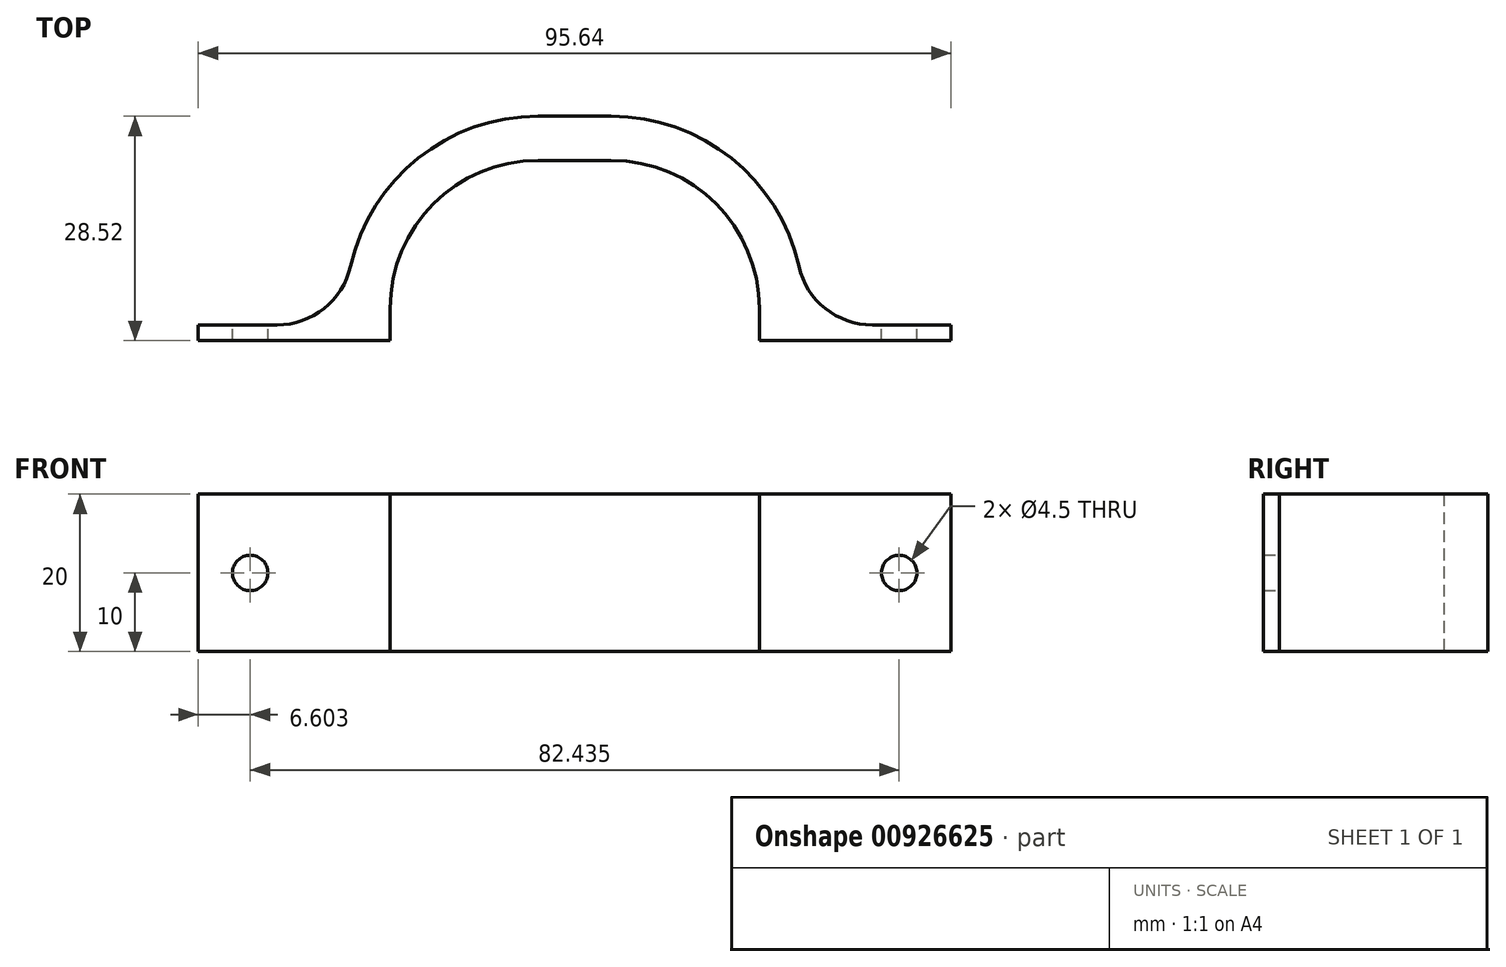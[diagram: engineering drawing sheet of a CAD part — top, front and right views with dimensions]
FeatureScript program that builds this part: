
annotation { "Feature Type Name" : "Feature", "Feature Type Description" : "" }
export const myFeature = defineFeature(function(context is Context, id is Id, definition is map)
    precondition{}
    {
        {
            var Q0;
            Q0=qCreatedBy(makeId("Top.planeOp"),FACE);
            var sketch = newSketch(context, id + "F0", { "sketchPlane" : qUnion([Q0])});
            skLineSegment(sketch, "E0", {"start": v(-45.82, -7.47) * mm, "end": v(-37.82, -7.47) * mm});
            skArc(sketch, "E1", {"start": v(-37.82, -7.47) * mm, "mid": v(-31.84, -5.37) * mm, "end": v(-28.47, 0) * mm});
            skArc(sketch, "E2", {"start": v(-4.65, 19.05) * mm, "mid": v(-19.9, 13.7) * mm, "end": v(-28.47, 0) * mm});
            skLineSegment(sketch, "E3", {"start": v(-4.65, 13.43) * mm, "end": v(0, 13.43) * mm});
            skLineSegment(sketch, "E4", {"start": v(-4.65, 19.05) * mm, "end": v(0, 19.05) * mm});
            skLineSegment(sketch, "E5", {"start": v(0, 24.2) * mm, "end": v(0, -23) * mm, "construction": true});
            skLineSegment(sketch, "E6.MirrorCS", {"start": v(4.65, 19.05) * mm, "end": v(0, 19.05) * mm});
            skLineSegment(sketch, "E7.MirrorCS", {"start": v(4.65, 13.43) * mm, "end": v(0, 13.43) * mm});
            skArc(sketch, "E8.MirrorCS", {"start": v(4.65, 19.05) * mm, "mid": v(19.9, 13.7) * mm, "end": v(28.47, 0) * mm});
            skArc(sketch, "E9.MirrorCS", {"start": v(37.82, -7.47) * mm, "mid": v(31.84, -5.37) * mm, "end": v(28.47, 0) * mm});
            skLineSegment(sketch, "E10.MirrorCS", {"start": v(45.82, -7.47) * mm, "end": v(37.82, -7.47) * mm});
            skPoint(sketch, "E11.orphan", {"position": v(23.45, -9.47) * mm});
            skPoint(sketch, "E12", {"position": v(-23.64, -5) * mm});
            skPoint(sketch, "E13", {"position": v(23.64, -5) * mm});
            skLineSegment(sketch, "E14", {"start": v(-23.45, -7.89) * mm, "end": v(-23.45, -9.47) * mm});
            skLineSegment(sketch, "E15", {"start": v(-23.45, -9.47) * mm, "end": v(-28.84, -9.47) * mm});
            skLineSegment(sketch, "E16", {"start": v(23.45, -7.89) * mm, "end": v(23.45, -9.47) * mm});
            skLineSegment(sketch, "E17", {"start": v(28.84, -9.47) * mm, "end": v(23.45, -9.47) * mm});
            skLineSegment(sketch, "E18", {"start": v(-23.45, -9.47) * mm, "end": v(27.28, -9.47) * mm, "construction": true});
            skPoint(sketch, "E19.MirrorCS.start.orphan", {"position": v(4.65, 13.43) * mm});
            skLineSegment(sketch, "E20", {"start": v(23.45, -7.89) * mm, "end": v(23.45, -5.37) * mm});
            skPoint(sketch, "E20.endSnap0", {"position": v(-31.84, -5.37) * mm});
            skArc(sketch, "E21", {"start": v(23.45, -5.37) * mm, "mid": v(17.94, 7.92) * mm, "end": v(4.65, 13.43) * mm});
            skLineSegment(sketch, "E22", {"start": v(-23.45, -7.89) * mm, "end": v(-23.45, -5.37) * mm});
            skArc(sketch, "E23", {"start": v(-4.65, 13.43) * mm, "mid": v(-17.94, 7.92) * mm, "end": v(-23.45, -5.37) * mm});
            skPoint(sketch, "E24.start.orphan", {"position": v(-45.39, -9.47) * mm});
            skLineSegment(sketch, "E25", {"start": v(-45.82, -7.47) * mm, "end": v(-45.82, -9.47) * mm});
            skLineSegment(sketch, "E26", {"start": v(-45.82, -9.47) * mm, "end": v(-28.84, -9.47) * mm});
            skPoint(sketch, "E27.MirrorCS.end.orphan", {"position": v(45.82, -7.47) * mm});
            skPoint(sketch, "E27.MirrorCS.start.orphan", {"position": v(45.39, -9.47) * mm});
            skLineSegment(sketch, "E28", {"start": v(45.82, -7.47) * mm, "end": v(45.82, -9.47) * mm});
            skLineSegment(sketch, "E29", {"start": v(45.82, -9.47) * mm, "end": v(28.84, -9.47) * mm});
            skSolve(sketch);
        }
        {
            var Q0;
            Q0=makeQuery(id+"F0.imprint","IMPRINT",FACE,{"disambiguationData":[TD([[makeQuery(id+"F0.imprint","IMPRINT",EDGE,{"derivedFrom":sQuery(id+"F0.wireOp",EDGE,"E0")}),-1.0]])]});
            extrude(context, id + "F1", {"entities" : qUnion([Q0]), "depth" : 20 * mm, "offsetDistance" : 25 * mm});
        }
        {
            var Q0;
            Q0=makeQuery(id+"F1.opExtrude","SWEPT_FACE",FACE,{"disambiguationData":[OSD([sQuery(id+"F0.wireOp",EDGE,"E0")])]});
            var sketch = newSketch(context, id + "F2", { "sketchPlane" : qUnion([Q0])});
            skCircle(sketch, "E30", {"center": v(41.22, 10) * mm, "radius": 2.32 * mm});
            skPoint(sketch, "E30.centerSnap0", {"position": v(37.82, 10) * mm});
            skCircle(sketch, "E31.MirrorC", {"center": v(-41.22, 10) * mm, "radius": 2.32 * mm});
            skSolve(sketch);
        }
        {
            var Q0;
            Q0=sQuery(id+"F2.wireOp",VERTEX,"E31.MirrorC.center");
            var Q1;
            Q1=makeQuery(id+"F1.opExtrude","SWEPT_BODY",BODY,{"disambiguationData":[OSD([sQuery(id+"F0.wireOp",EDGE,"E0"),sQuery(id+"F0.wireOp",EDGE,"E1"),sQuery(id+"F0.wireOp",EDGE,"E2"),sQuery(id+"F0.wireOp",EDGE,"uV92Ddhu-M5Bt-vWS1-TbGC-g9NzF9XPtX7C"),sQuery(id+"F0.wireOp",EDGE,"E24"),sQuery(id+"F0.wireOp",EDGE,"E3"),sQuery(id+"F0.wireOp",EDGE,"E4"),sQuery(id+"F0.wireOp",EDGE,"0Qwv5SWm-8QDR-l9fD-u0Jv-9uYLpRH72VuP"),sQuery(id+"F0.wireOp",EDGE,"MbMYqxt5-BfHK-vX8P-ZZeJ-HiYTgc9mHEWE"),sQuery(id+"F0.wireOp",EDGE,"E6.MirrorCS"),sQuery(id+"F0.wireOp",EDGE,"E7.MirrorCS"),sQuery(id+"F0.wireOp",EDGE,"E19.MirrorCS"),sQuery(id+"F0.wireOp",EDGE,"E8.MirrorCS"),sQuery(id+"F0.wireOp",EDGE,"E9.MirrorCS"),sQuery(id+"F0.wireOp",EDGE,"E10.MirrorCS"),sQuery(id+"F0.wireOp",EDGE,"E27.MirrorCS"),sQuery(id+"F0.wireOp",EDGE,"ffb70a82-99cb-465d-b67c-bdc7b6a140d00.MirrorCS"),sQuery(id+"F0.wireOp",EDGE,"f730d3b3-40b3-4068-a242-c0ff46c35bcd0.MirrorCS")])]});
            hole(context, id + "F3", {"style" : HoleStyle.SIMPLE, "endStyle" : HoleEndStyle.THROUGH, "holeDiameter" : 4.5 * mm, "majorDiameter" : 5 * mm, "isTappedThrough" : true, "tappedDepth" : 12 * mm, "tapClearance" : 3, "locations" : qUnion([Q0]), "scope" : qUnion([Q1])});
        }
        {
            var Q0;
            Q0=sQuery(id+"F2.wireOp",VERTEX,"E30.center");
            var Q1;
            Q1=makeQuery(id+"F1.opExtrude","SWEPT_BODY",BODY,{"disambiguationData":[OSD([sQuery(id+"F0.wireOp",EDGE,"E0"),sQuery(id+"F0.wireOp",EDGE,"E1"),sQuery(id+"F0.wireOp",EDGE,"E2"),sQuery(id+"F0.wireOp",EDGE,"uV92Ddhu-M5Bt-vWS1-TbGC-g9NzF9XPtX7C"),sQuery(id+"F0.wireOp",EDGE,"E24"),sQuery(id+"F0.wireOp",EDGE,"E3"),sQuery(id+"F0.wireOp",EDGE,"E4"),sQuery(id+"F0.wireOp",EDGE,"0Qwv5SWm-8QDR-l9fD-u0Jv-9uYLpRH72VuP"),sQuery(id+"F0.wireOp",EDGE,"MbMYqxt5-BfHK-vX8P-ZZeJ-HiYTgc9mHEWE"),sQuery(id+"F0.wireOp",EDGE,"E6.MirrorCS"),sQuery(id+"F0.wireOp",EDGE,"E7.MirrorCS"),sQuery(id+"F0.wireOp",EDGE,"E19.MirrorCS"),sQuery(id+"F0.wireOp",EDGE,"E8.MirrorCS"),sQuery(id+"F0.wireOp",EDGE,"E9.MirrorCS"),sQuery(id+"F0.wireOp",EDGE,"E10.MirrorCS"),sQuery(id+"F0.wireOp",EDGE,"E27.MirrorCS"),sQuery(id+"F0.wireOp",EDGE,"ffb70a82-99cb-465d-b67c-bdc7b6a140d00.MirrorCS"),sQuery(id+"F0.wireOp",EDGE,"f730d3b3-40b3-4068-a242-c0ff46c35bcd0.MirrorCS")])]});
            hole(context, id + "F4", {"style" : HoleStyle.SIMPLE, "endStyle" : HoleEndStyle.THROUGH, "holeDiameter" : 4.5 * mm, "majorDiameter" : 5 * mm, "isTappedThrough" : true, "tappedDepth" : 12 * mm, "tapClearance" : 3, "locations" : qUnion([Q0]), "scope" : qUnion([Q1])});
        }
        {
            var Q0;
            Q0=makeQuery(id+"F1.opExtrude","SWEPT_FACE",FACE,{"disambiguationData":[OSD([sQuery(id+"F0.wireOp",EDGE,"E25")])]});
            extrude(context, id + "F5", {"entities" : qUnion([Q0]), "operationType" : NewBodyOperationType.ADD, "depth" : 2 * mm, "offsetDistance" : 25 * mm});
        }
        {
            var Q0;
            Q0=makeQuery(id+"F1.opExtrude","SWEPT_FACE",FACE,{"disambiguationData":[OSD([sQuery(id+"F0.wireOp",EDGE,"E28")])]});
            extrude(context, id + "F6", {"entities" : qUnion([Q0]), "operationType" : NewBodyOperationType.ADD, "depth" : 2 * mm, "offsetDistance" : 25 * mm});
        }
    });
